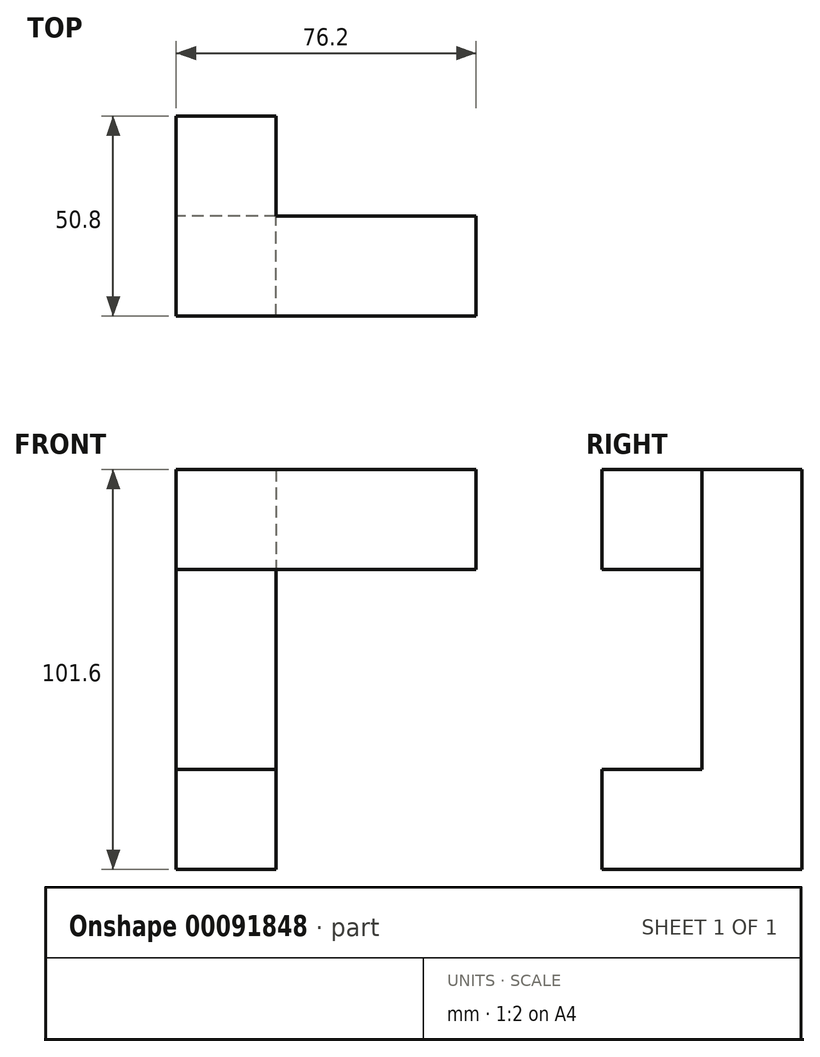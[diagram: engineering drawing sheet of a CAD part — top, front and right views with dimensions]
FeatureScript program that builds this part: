
annotation { "Feature Type Name" : "Feature", "Feature Type Description" : "" }
export const myFeature = defineFeature(function(context is Context, id is Id, definition is map)
    precondition{}
    {
        {
            var Q0;
            Q0=qCreatedBy(makeId("Right.planeOp"),FACE);
            var sketch = newSketch(context, id + "F0", { "sketchPlane" : qUnion([Q0])});
            skLineSegment(sketch, "E0.bottom", {"start": v(0, 101.6) * mm, "end": v(50.8, 101.6) * mm});
            skLineSegment(sketch, "E0.top", {"start": v(0, 0) * mm, "end": v(50.8, 0) * mm});
            skLineSegment(sketch, "E0.left", {"start": v(0, 101.6) * mm, "end": v(0, 0) * mm});
            skLineSegment(sketch, "E0.right", {"start": v(50.8, 101.6) * mm, "end": v(50.8, 0) * mm});
            skLineSegment(sketch, "E1.bottom", {"start": v(0, 76.2) * mm, "end": v(25.4, 76.2) * mm});
            skLineSegment(sketch, "E1.top", {"start": v(0, 25.4) * mm, "end": v(25.4, 25.4) * mm});
            skLineSegment(sketch, "E1.left", {"start": v(0, 76.2) * mm, "end": v(0, 25.4) * mm});
            skLineSegment(sketch, "E1.right", {"start": v(25.4, 76.2) * mm, "end": v(25.4, 25.4) * mm});
            skSolve(sketch);
        }
        {
            var Q0;
            {var subQ4=sQuery(id+"F0.wireOp",EDGE,"E0.bottom");Q0=makeQuery(id+"F0.imprint","IMPRINT",FACE,{"disambiguationData":[TD([[makeQuery(id+"F0.imprint","IMPRINT",EDGE,{"derivedFrom":subQ4}),-1.0]])]});}
            extrude(context, id + "F1", {"entities" : qUnion([Q0]), "depth" : 25.4 * mm});
        }
        {
            var Q0;
            Q0=makeQuery(id+"F1.opExtrude","CAP_FACE",FACE,{"disambiguationData":[OSD([sQuery(id+"F0.wireOp",EDGE,"E0.bottom"),sQuery(id+"F0.wireOp",EDGE,"E0.top"),sQuery(id+"F0.wireOp",EDGE,"E0.left"),sQuery(id+"F0.wireOp",EDGE,"E0.right"),sQuery(id+"F0.wireOp",EDGE,"E1.bottom"),sQuery(id+"F0.wireOp",EDGE,"E1.top"),sQuery(id+"F0.wireOp",EDGE,"E1.right")])],"isStart":false});
            var sketch = newSketch(context, id + "F2", { "sketchPlane" : qUnion([Q0])});
            skLineSegment(sketch, "E2.bottom", {"start": v(0, 101.6) * mm, "end": v(25.4, 101.6) * mm});
            skLineSegment(sketch, "E2.top", {"start": v(0, 76.2) * mm, "end": v(25.4, 76.2) * mm});
            skLineSegment(sketch, "E2.left", {"start": v(0, 101.6) * mm, "end": v(0, 76.2) * mm});
            skLineSegment(sketch, "E2.right", {"start": v(25.4, 101.6) * mm, "end": v(25.4, 76.2) * mm});
            skSolve(sketch);
        }
        {
            var Q0;
            Q0 = qSketchRegion(id + "F2", true);
            extrude(context, id + "F3", {"entities" : qUnion([Q0]), "operationType" : NewBodyOperationType.ADD, "depth" : 50.8 * mm});
        }
    });
